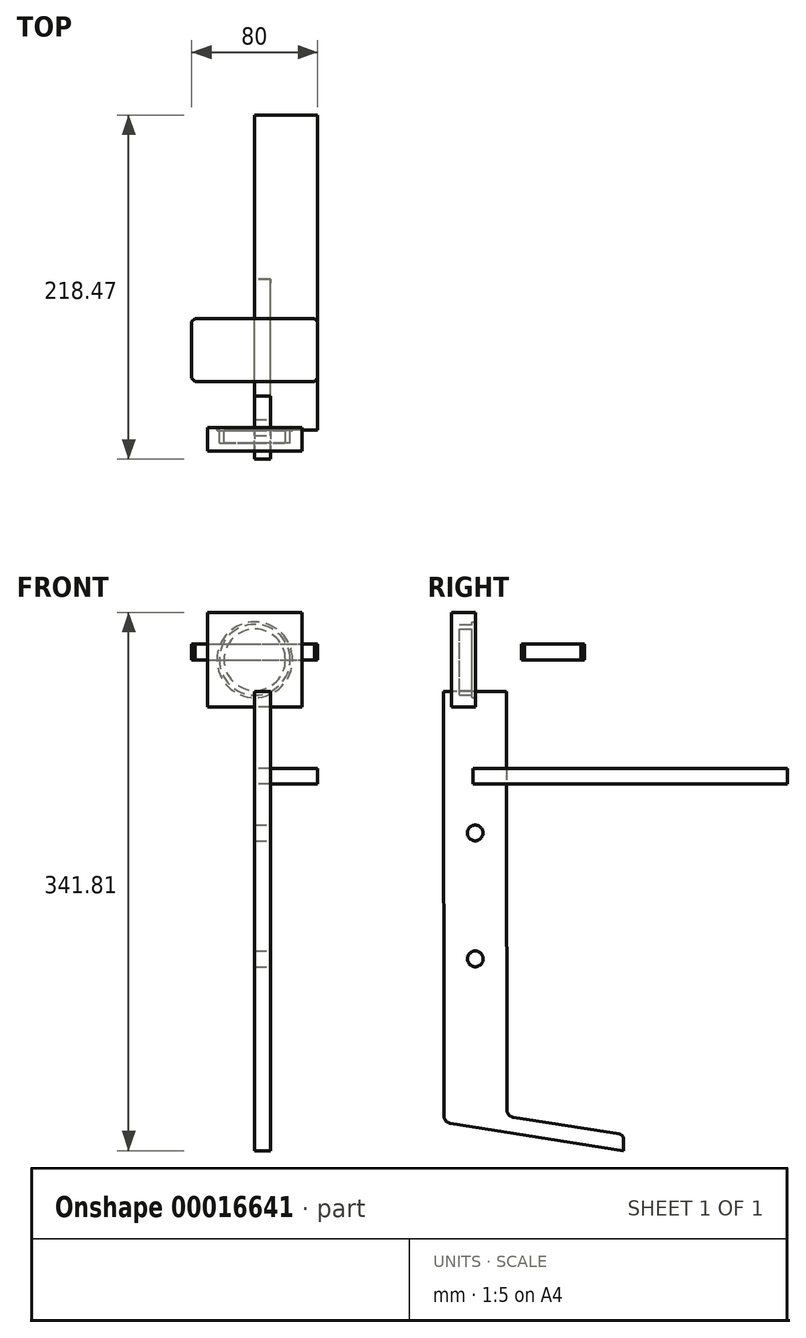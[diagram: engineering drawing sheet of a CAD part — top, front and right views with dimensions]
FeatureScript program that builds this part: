
annotation { "Feature Type Name" : "Feature", "Feature Type Description" : "" }
export const myFeature = defineFeature(function(context is Context, id is Id, definition is map)
    precondition{}
    {
        {
            var Q0;
            Q0=qCreatedBy(makeId("Front.planeOp"),FACE);
            var sketch = newSketch(context, id + "F0", { "sketchPlane" : qUnion([Q0])});
            skCircle(sketch, "E0", {"center": v(0, 0) * mm, "radius": 24 * mm});
            skSolve(sketch);
        }
        {
            var Q0;
            Q0 = qSketchRegion(id + "F0", true);
            extrude(context, id + "F1", {"entities" : qUnion([Q0]), "depth" : 2 * mm});
        }
        {
            var Q0;
            Q0=makeQuery(id+"F1.opExtrude","CAP_FACE",FACE,{"disambiguationData":[OSD([sQuery(id+"F0.wireOp",EDGE,"E0")])],"isStart":false});
            var sketch = newSketch(context, id + "F2", { "sketchPlane" : qUnion([Q0])});
            skCircle(sketch, "E1", {"center": v(0, 0) * mm, "radius": 22.5 * mm});
            skCircle(sketch, "E2", {"center": v(0, 0) * mm, "radius": 19.48 * mm});
            skSolve(sketch);
        }
        {
            var Q0;
            Q0 = qSketchRegion(id + "F2", true);
            extrude(context, id + "F3", {"entities" : qUnion([Q0]), "operationType" : NewBodyOperationType.ADD, "depth" : 8 * mm});
        }
        {
            var Q0;
            Q0=qCreatedBy(makeId("Front.planeOp"),FACE);
            var sketch = newSketch(context, id + "F4", { "sketchPlane" : qUnion([Q0])});
            skLineSegment(sketch, "E3.rect.bottom", {"start": v(30, 30) * mm, "end": v(-30, 30) * mm});
            skLineSegment(sketch, "E3.rect.top", {"start": v(30, -30) * mm, "end": v(-30, -30) * mm});
            skLineSegment(sketch, "E3.rect.left", {"start": v(30, 30) * mm, "end": v(30, -30) * mm});
            skLineSegment(sketch, "E3.rect.right", {"start": v(-30, 30) * mm, "end": v(-30, -30) * mm});
            skPoint(sketch, "E3.rect.middle", {"position": v(0, 0) * mm});
            skSolve(sketch);
        }
        {
            var Q0;
            Q0 = qSketchRegion(id + "F4", true);
            extrude(context, id + "F5", {"entities" : qUnion([Q0]), "depth" : 15 * mm});
        }
        {
            var Q0;
            Q0=qCreatedBy(makeId("Top.planeOp"),FACE);
            var sketch = newSketch(context, id + "F6", { "sketchPlane" : qUnion([Q0])});
            skLineSegment(sketch, "E4.rect.bottom", {"start": v(-40, 29.23) * mm, "end": v(40, 29.23) * mm});
            skLineSegment(sketch, "E4.rect.top", {"start": v(-40, 69.23) * mm, "end": v(40, 69.23) * mm});
            skLineSegment(sketch, "E4.rect.left", {"start": v(-40, 29.23) * mm, "end": v(-40, 69.23) * mm});
            skLineSegment(sketch, "E4.rect.right", {"start": v(40, 29.23) * mm, "end": v(40, 69.23) * mm});
            skPoint(sketch, "E4.rect.middle", {"position": v(0, 49.23) * mm});
            skSolve(sketch);
        }
        {
            var Q0;
            Q0 = qSketchRegion(id + "F6", true);
            extrude(context, id + "F7", {"entities" : qUnion([Q0]), "depth" : 10 * mm});
        }
        {
            var Q0;
            Q0=makeQuery(id+"F7.opExtrude","SWEPT_EDGE",EDGE,{"disambiguationData":[OSD([sQuery(id+"F6.wireOp",EDGE,"E4.rect.top"),sQuery(id+"F6.wireOp",EDGE,"E4.rect.left")])]});
            var Q1;
            Q1=makeQuery(id+"F7.opExtrude","SWEPT_EDGE",EDGE,{"disambiguationData":[OSD([sQuery(id+"F6.wireOp",EDGE,"E4.rect.bottom"),sQuery(id+"F6.wireOp",EDGE,"E4.rect.left")])]});
            var Q2;
            Q2=makeQuery(id+"F7.opExtrude","SWEPT_EDGE",EDGE,{"disambiguationData":[OSD([sQuery(id+"F6.wireOp",EDGE,"E4.rect.top"),sQuery(id+"F6.wireOp",EDGE,"E4.rect.right")])]});
            var Q3;
            Q3=makeQuery(id+"F7.opExtrude","SWEPT_EDGE",EDGE,{"disambiguationData":[OSD([sQuery(id+"F6.wireOp",EDGE,"E4.rect.bottom"),sQuery(id+"F6.wireOp",EDGE,"E4.rect.right")])]});
            chamfer(context, id + "F8", {"entities" : qUnion([Q0, Q1, Q2, Q3]), "width" : 2 * mm, "tangentPropagation" : true});
        }
        {
            var Q0;
            Q0=qCreatedBy(makeId("Right.planeOp"),FACE);
            var sketch = newSketch(context, id + "F9", { "sketchPlane" : qUnion([Q0])});
            skLineSegment(sketch, "E5.rect.bottom", {"start": v(19.94, -20) * mm, "end": v(-20.06, -20) * mm});
            skLineSegment(sketch, "E5.rect.left", {"start": v(19.94, -20) * mm, "end": v(20.06, -285.73) * mm});
            skLineSegment(sketch, "E5.rect.right", {"start": v(-20.06, -20) * mm, "end": v(-19.94, -289.54) * mm});
            skPoint(sketch, "E5.rect.middle", {"position": v(0, -155) * mm});
            skLineSegment(sketch, "E6", {"start": v(24.28, -290.67) * mm, "end": v(91.6, -301.3) * mm});
            skLineSegment(sketch, "E7.0", {"start": v(-15.72, -294.47) * mm, "end": v(94.07, -311.8) * mm});
            skPoint(sketch, "E5.rect.top.end.orphan", {"position": v(-19.94, -290) * mm});
            skLineSegment(sketch, "E8", {"start": v(94.07, -311.8) * mm, "end": v(94.13, -304.28) * mm});
            skPoint(sketch, "E9.visualSharp", {"position": v(20.06, -290) * mm});
            skArc(sketch, "E9.filletArc", {"start": v(20.06, -285.73) * mm, "mid": v(21.26, -288.98) * mm, "end": v(24.28, -290.67) * mm});
            skPoint(sketch, "E10.visualSharp", {"position": v(-19.93, -293.8) * mm});
            skArc(sketch, "E10.filletArc", {"start": v(-19.94, -289.54) * mm, "mid": v(-18.74, -292.78) * mm, "end": v(-15.72, -294.47) * mm});
            skPoint(sketch, "E11.visualSharp", {"position": v(94.15, -301.7) * mm});
            skArc(sketch, "E11.filletArc", {"start": v(94.13, -304.28) * mm, "mid": v(93.41, -302.32) * mm, "end": v(91.6, -301.3) * mm});
            skSolve(sketch);
        }
        {
            var Q0;
            Q0 = qSketchRegion(id + "F9", true);
            extrude(context, id + "F10", {"entities" : qUnion([Q0]), "depth" : 10 * mm});
        }
        {
            var Q0;
            Q0=makeQuery(id+"F10.opExtrude","CAP_FACE",FACE,{"disambiguationData":[OSD([sQuery(id+"F9.wireOp",EDGE,"E5.rect.bottom"),sQuery(id+"F9.wireOp",EDGE,"E5.rect.left"),sQuery(id+"F9.wireOp",EDGE,"E5.rect.right"),sQuery(id+"F9.wireOp",EDGE,"E6"),sQuery(id+"F9.wireOp",EDGE,"E7.0"),sQuery(id+"F9.wireOp",EDGE,"E8"),sQuery(id+"F9.wireOp",EDGE,"E9.filletArc"),sQuery(id+"F9.wireOp",EDGE,"E10.filletArc"),sQuery(id+"F9.wireOp",EDGE,"E11.filletArc")])],"isStart":false});
            var sketch = newSketch(context, id + "F11", { "sketchPlane" : qUnion([Q0])});
            skCircle(sketch, "E12", {"center": v(-0.06, -110) * mm, "radius": 5 * mm});
            skPoint(sketch, "E12.centerSnap0", {"position": v(-0.06, -20) * mm});
            skCircle(sketch, "E13", {"center": v(0, -190) * mm, "radius": 5 * mm});
            skSolve(sketch);
        }
        {
            var Q0;
            Q0 = qSketchRegion(id + "F11", true);
            extrude(context, id + "F12", {"entities" : qUnion([Q0]), "operationType" : NewBodyOperationType.REMOVE, "oppositeDirection" : true, "depth" : 25 * mm});
        }
        {
            var Q0;
            Q0=qCreatedBy(makeId("Right.planeOp"),FACE);
            var sketch = newSketch(context, id + "F13", { "sketchPlane" : qUnion([Q0])});
            skLineSegment(sketch, "E14.bottom", {"start": v(-1.6, -78.93) * mm, "end": v(198.4, -78.93) * mm});
            skLineSegment(sketch, "E14.top", {"start": v(-1.6, -68.93) * mm, "end": v(198.4, -68.93) * mm});
            skLineSegment(sketch, "E14.left", {"start": v(-1.6, -78.93) * mm, "end": v(-1.6, -68.93) * mm});
            skLineSegment(sketch, "E14.right", {"start": v(198.4, -78.93) * mm, "end": v(198.4, -68.93) * mm});
            skSolve(sketch);
        }
        {
            var Q0;
            Q0 = qSketchRegion(id + "F13", true);
            extrude(context, id + "F14", {"entities" : qUnion([Q0]), "depth" : 40 * mm});
        }
    });
